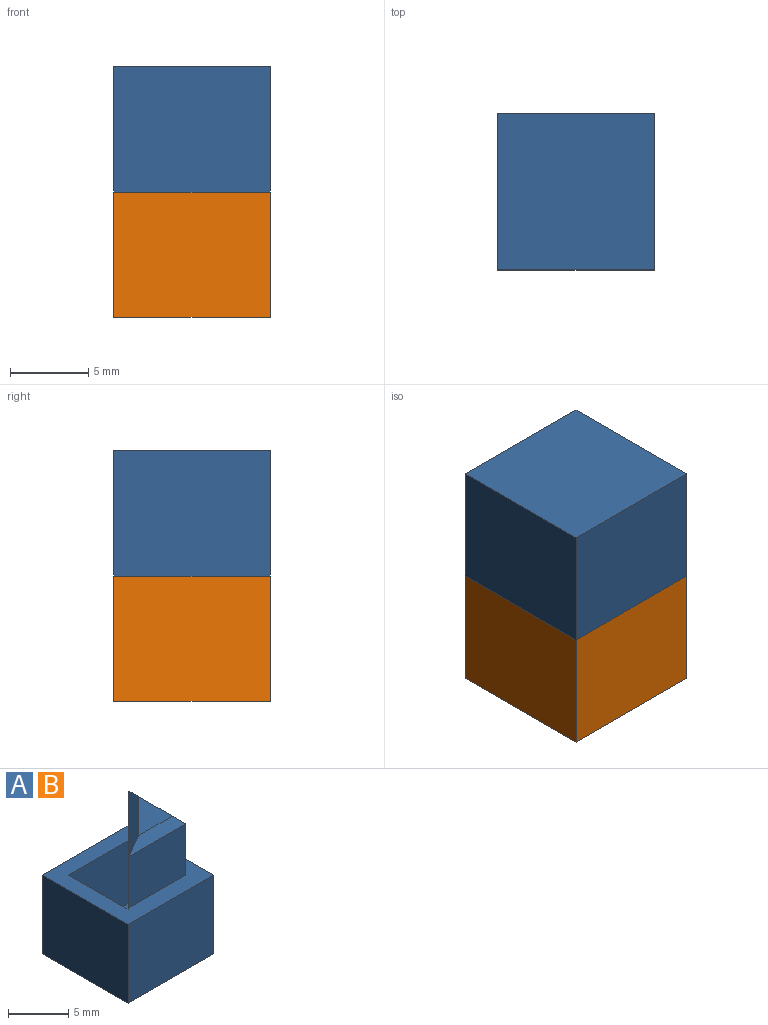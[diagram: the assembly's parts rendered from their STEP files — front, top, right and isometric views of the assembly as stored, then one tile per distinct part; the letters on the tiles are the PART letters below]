
ASSEMBLY  parts=2 mates=1
PART A: 17 faces, bbox 10x10x14 mm
  f0: plane 10x10mm, normal (0,0,1), area 53.5mm2, adj f1,f2,f3,f4,f7,f8,f9,f11
  f1: plane 10x8mm, normal (-1,0,0), area 80mm2, adj f0,f2,f4,f5
  f2: plane 10x8mm, normal (0,-1,0), area 80mm2, adj f0,f1,f3,f5
  f3: plane 10x8mm, normal (1,0,0), area 80mm2, adj f0,f2,f4,f5
  f4: plane 10x8mm, normal (0,1,0), area 80mm2, adj f0,f1,f3,f5
  f5: plane 10x10mm, normal (0,0,-1), area 100mm2, adj f1,f2,f3,f4
  f6: plane 6.94x6.94mm, normal (0,0,1), area 24.1mm2, adj f7,f8,f9
  f7: plane 6.94x6.94mm, normal (-0.71,0.71,0), area 62.8mm2, adj f0,f6,f8,f9
  f8: plane 6.94x6.4mm, normal (0,-1,0), area 44.4mm2, adj f0,f6,f7,f9
  f9: plane 6.94x6.4mm, normal (1,0,0), area 44.4mm2, adj f0,f6,f7,f8
  f10: plane 3.97x3.97mm, normal (0,0,1), area 7.9mm2, adj f14,f15,f16
  f11: plane 6.7x6.7mm, normal (-0.71,0.71,0), area 49.3mm2, adj f0,f12,f13,f16
  f12: plane 6.7x5.2mm, normal (0,-1,0), area 34.8mm2, adj f0,f11,f13,f14
  f13: plane 6.7x5.2mm, normal (1,0,0), area 34.8mm2, adj f0,f11,f12,f15
  f14: plane 6.7x0.8mm, normal (0,-0.71,0.71), area 6mm2, adj f10,f12,f15,f16
  f15: plane 6.7x0.8mm, normal (0.71,0,0.71), area 6mm2, adj f10,f13,f14,f16
  f16: plane 6.7x6.7mm, normal (-0.5,0.5,0.71), area 8.5mm2, adj f10,f11,f14,f15
PART B: same geometry as A
PLACE A rot(axis=(-0.71,-0.71,0),180deg) t=(0,0,16)mm
PLACE B at identity
MATE fastened A.f4 <-> B.f3  axis (1,0,0) through (10,5,8)mm
